# Revit family: Ceileo-SQ
name_source: partatom
category: Lighting Fixtures
units: mm (PartAtom-declared; Revit-internal decimal feet)

## family parameters
Cut with Voids When Loaded = No
Host = Face
Light Source = No
OmniClass Number = 23.80.70.11
OmniClass Title = Luminaries for Internal Lighting
Part Type = Normal
Room Calculation Point = No
Round Connector Dimension = Use Diameter
Shared = No

## types (12) — shared parameters
Apparent Load = 55 VA
Default Elevation = 48"
Description = Ceileo is a commercial grade LED canopy luminaire that utilizes high powered LED’s with precise efficient optical control and on board wattage and lumen choices.
Glass = White Glass
Lamp = LED Lamp
Manufacturer = Beacon Products
Model = CLO SQ
Nominal Watts = 55 W
URL = https://www.currentlighting.com
Voltage = 120 V

## per-type parameters (varying)
| type | Backbox | Photometric Web |
| CLO SQ-BBT | Paint- Black Textured | Web CLO : CLO-24NB-55-3K-5X5 |
| CLO SQ-BMT | Paint- Black Matte Textured | Web CLO : CLO-24NB-55-3K-5X5 |
| CLO SQ-WHT | Paint- White | Web CLO : CLO-24NB-55-3K-5X5 |
| CLO SQ-BZT | Paint- Bronze Textured | Web CLO : CLO-24NB-55-5K-T5SQN |
| CLO SQ-MBT | Paint- Mettalic Bronze Textured | Web CLO : CLO-24NB-55-3K-5X5 |
| CLO SQ-DBT | Paint- Dark  Bronze Textured | Web CLO : CLO-24NB-55-3K-5X5 |
| CLO SQ-GYS | Paint- Grey smooth | Web CLO : CLO-24NB-55-3K-5X5 |
| CLO SQ-DPS | Paint- Dark Platinum Smooth | Web CLO : CLO-24NB-55-3K-5X5 |
| CLO SQ-GNT | Paint- Green Textured | Web CLO : CLO-24NB-55-3K-5X5 |
| CLO SQ-MST | Paint- Mettallic Silver Textured | Web CLO : CLO-24NB-55-3K-5X5 |
| CLO SQ-MTT | Paint- Metallic titanium textured | Web CLO : CLO-24NB-55-3K-5X5 |
| CLO SQ-OWI | Paint- Old World Iron | Web CLO : CLO-24NB-55-3K-5X5 |

## geometry (parser evidence)
native form markers: Blend x26, Sweep x5
no freeform markers — native parametric forms only
